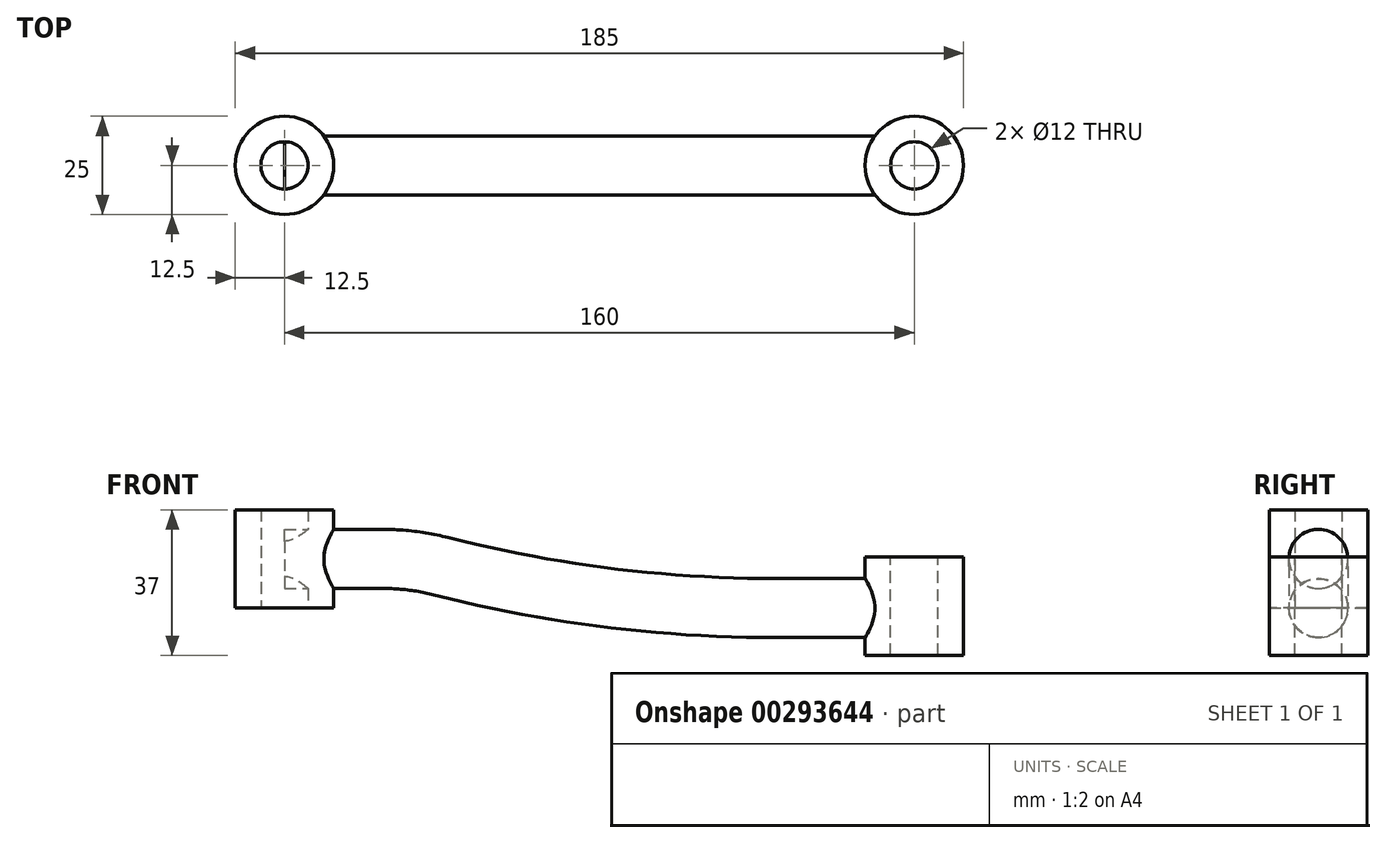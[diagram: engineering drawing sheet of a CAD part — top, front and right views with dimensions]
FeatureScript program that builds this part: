
annotation { "Feature Type Name" : "Feature", "Feature Type Description" : "" }
export const myFeature = defineFeature(function(context is Context, id is Id, definition is map)
    precondition{}
    {
        {
            var Q0;
            Q0=qCreatedBy(makeId("Front.planeOp"),FACE);
            var sketch = newSketch(context, id + "F0", { "sketchPlane" : qUnion([Q0])});
            skLineSegment(sketch, "E0", {"start": v(0, 0) * mm, "end": v(25, 0) * mm});
            skLineSegment(sketch, "E1", {"start": v(0, 0) * mm, "end": v(150, 0) * mm, "construction": true});
            skLineSegment(sketch, "E2", {"start": v(150, 0) * mm, "end": v(150, -12.5) * mm, "construction": true});
            skLineSegment(sketch, "E3", {"start": v(150, -12.5) * mm, "end": v(125, -12.5) * mm});
            skArc(sketch, "E4", {"start": v(25, 0) * mm, "mid": v(32.44, -0.46) * mm, "end": v(39.77, -1.85) * mm});
            skArc(sketch, "E5", {"start": v(125, -12.5) * mm, "mid": v(82.05, -9.83) * mm, "end": v(39.77, -1.85) * mm});
            skSolve(sketch);
        }
        {
            var Q0;
            Q0=qCreatedBy(makeId("Top.planeOp"),FACE);
            var sketch = newSketch(context, id + "F1", { "sketchPlane" : qUnion([Q0])});
            skCircle(sketch, "E6", {"center": v(0, 0) * mm, "radius": 12.5 * mm});
            skCircle(sketch, "E7", {"center": v(0, 0) * mm, "radius": 6 * mm});
            skSolve(sketch);
        }
        {
            var Q0;
            Q0=qCreatedBy(makeId("Right.planeOp"),FACE);
            cPlane(context, id + "F2", {"entities" : qUnion([Q0]), "cplaneType" : CPlaneType.OFFSET, "offset" : 10 * mm, "width" : 150 * mm, "height" : 150 * mm});
        }
        {
            var Q0;
            Q0=qCreatedBy(id+"F2.planeOp",FACE);
            var sketch = newSketch(context, id + "F3", { "sketchPlane" : qUnion([Q0])});
            skCircle(sketch, "E8", {"center": v(0, 0) * mm, "radius": 7.5 * mm});
            skSolve(sketch);
        }
        {
            var Q0;
            Q0=makeQuery(id+"F3.imprint","IMPRINT",FACE,{"disambiguationData":[TD([[makeQuery(id+"F3.imprint","IMPRINT",EDGE,{"derivedFrom":sQuery(id+"F3.wireOp",EDGE,"E8")}),1.0]])]});
            var Q1;
            Q1=sQuery(id+"F0.wireOp",EDGE,"E0");
            var Q2;
            Q2=sQuery(id+"F0.wireOp",EDGE,"E4");
            var Q3;
            Q3=sQuery(id+"F0.wireOp",EDGE,"E5");
            var Q4;
            Q4=sQuery(id+"F0.wireOp",EDGE,"E3");
            sweep(context, id + "F4", {"profiles" : qUnion([Q0]), "path" : qUnion([Q1, Q2, Q3, Q4])});
        }
        {
            var Q0;
            Q0=makeQuery(id+"F1.imprint","IMPRINT",FACE,{"disambiguationData":[TD([[makeQuery(id+"F1.imprint","IMPRINT",EDGE,{"derivedFrom":sQuery(id+"F1.wireOp",EDGE,"E6")}),1.0]])]});
            extrude(context, id + "F5", {"entities" : qUnion([Q0]), "operationType" : NewBodyOperationType.ADD, "endBound" : BoundingType.SYMMETRIC, "depth" : 25 * mm});
        }
        {
            var Q0;
            Q0=qCreatedBy(makeId("Top.planeOp"),FACE);
            cPlane(context, id + "F6", {"entities" : qUnion([Q0]), "cplaneType" : CPlaneType.OFFSET, "offset" : 12 * mm, "oppositeDirection" : true, "width" : 150 * mm, "height" : 150 * mm});
        }
        {
            var Q0;
            Q0=qCreatedBy(id+"F6.planeOp",FACE);
            var sketch = newSketch(context, id + "F7", { "sketchPlane" : qUnion([Q0])});
            skLineSegment(sketch, "E9", {"start": v(160, -7.5) * mm, "end": v(135, -7.5) * mm});
            skLineSegment(sketch, "E10", {"start": v(135, 7.5) * mm, "end": v(160, 7.5) * mm});
            skLineSegment(sketch, "E11", {"start": v(160, -7.5) * mm, "end": v(160, 7.5) * mm});
            skCircle(sketch, "E12", {"center": v(160, 0) * mm, "radius": 12.5 * mm});
            skSolve(sketch);
        }
        {
            var Q0;
            Q0 = qSketchRegion(id + "F7", true);
            extrude(context, id + "F8", {"entities" : qUnion([Q0]), "operationType" : NewBodyOperationType.ADD, "endBound" : BoundingType.SYMMETRIC, "depth" : 25 * mm});
        }
        {
            var Q0;
            Q0=makeQuery(id+"F8.opExtrude","CAP_FACE",FACE,{"disambiguationData":[OSD([sQuery(id+"F7.wireOp",EDGE,"E12")])],"isStart":false});
            var sketch = newSketch(context, id + "F9", { "sketchPlane" : qUnion([Q0])});
            skCircle(sketch, "E13.0", {"center": v(160, 0) * mm, "radius": 12.5 * mm});
            skCircle(sketch, "E14", {"center": v(160, 0) * mm, "radius": 6 * mm});
            skSolve(sketch);
        }
        {
            var Q0;
            Q0=makeQuery(id+"F9.imprint","IMPRINT",FACE,{"disambiguationData":[TD([[makeQuery(id+"F9.imprint","IMPRINT",EDGE,{"derivedFrom":sQuery(id+"F9.wireOp",EDGE,"E14")}),1.0]])]});
            extrude(context, id + "F10", {"entities" : qUnion([Q0]), "operationType" : NewBodyOperationType.REMOVE, "oppositeDirection" : true, "depth" : 25 * mm});
        }
    });
